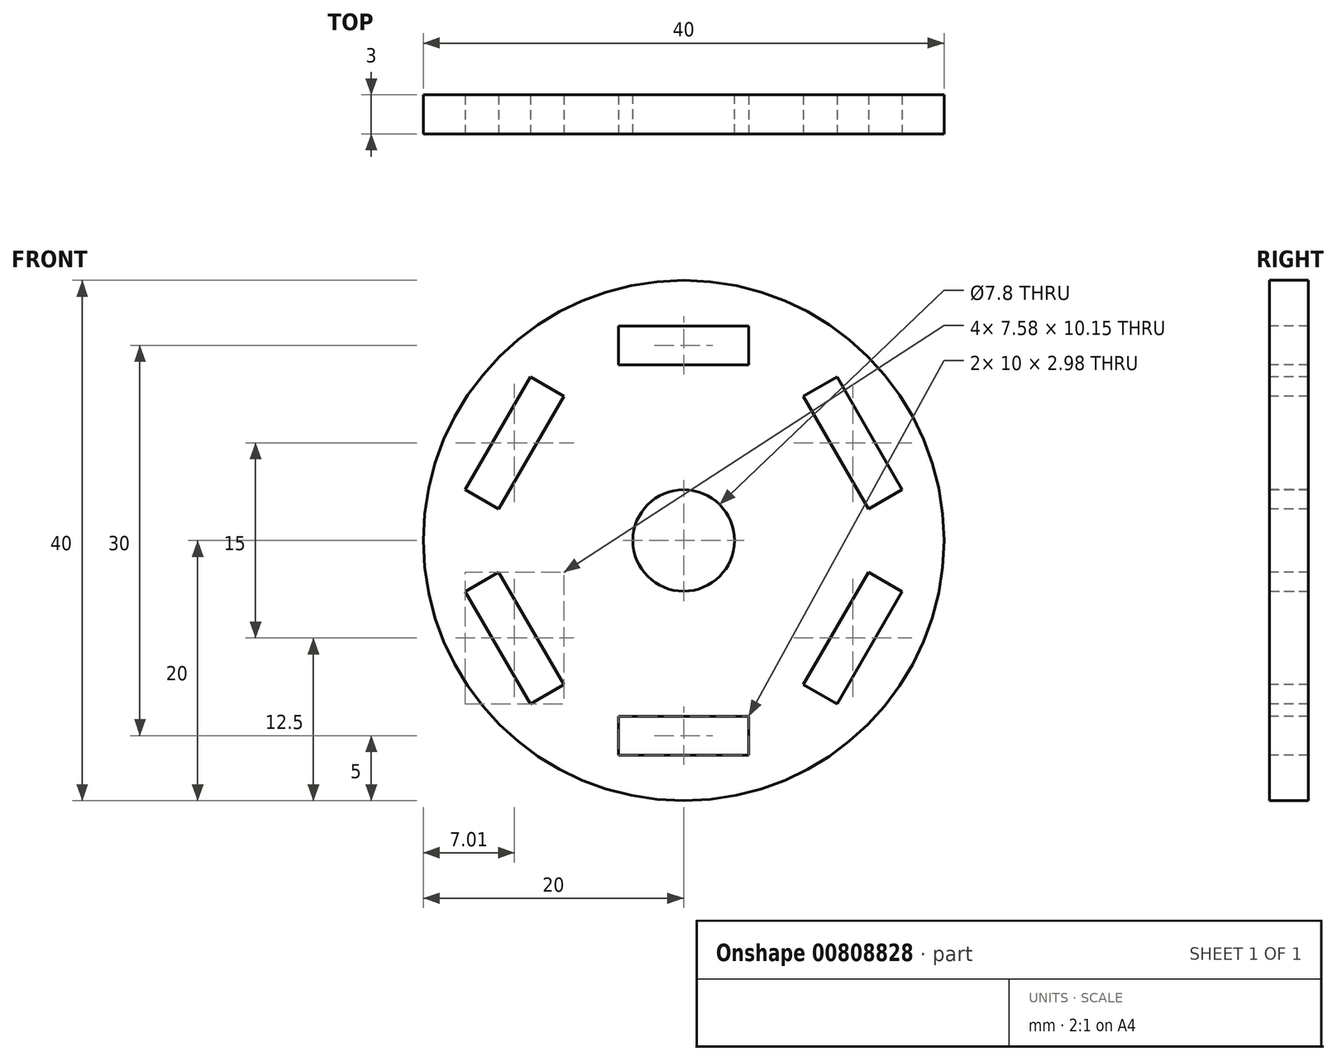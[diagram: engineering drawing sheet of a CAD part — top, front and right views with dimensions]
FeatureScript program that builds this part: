
annotation { "Feature Type Name" : "Feature", "Feature Type Description" : "" }
export const myFeature = defineFeature(function(context is Context, id is Id, definition is map)
    precondition{}
    {
        {
            var Q0;
            Q0=qCreatedBy(makeId("Front.planeOp"),FACE);
            var sketch = newSketch(context, id + "F0", { "sketchPlane" : qUnion([Q0])});
            skCircle(sketch, "E0", {"center": v(0, 0) * mm, "radius": 20 * mm});
            skCircle(sketch, "E1", {"center": v(0, 0) * mm, "radius": 3.9 * mm});
            skSolve(sketch);
        }
        {
            var Q0;
            Q0=qSketchRegion(id+"F0",true);
            extrude(context, id + "F1", {"entities" : qUnion([Q0]), "depth" : 3 * mm, "offsetDistance" : 25 * mm});
        }
        {
            var Q0;
            Q0=makeQuery(id+"F1.opExtrude","CAP_FACE",FACE,{"disambiguationData":[OSD([sQuery(id+"F0.wireOp",EDGE,"E0"),sQuery(id+"F0.wireOp",EDGE,"E1")])],"isStart":false});
            var sketch = newSketch(context, id + "F2", { "sketchPlane" : qUnion([Q0])});
            skLineSegment(sketch, "E2.bottom", {"start": v(-5, -13.5) * mm, "end": v(5, -13.5) * mm});
            skLineSegment(sketch, "E2.top", {"start": v(-5, -16.49) * mm, "end": v(5, -16.49) * mm});
            skLineSegment(sketch, "E2.left", {"start": v(-5, -13.5) * mm, "end": v(-5, -16.49) * mm});
            skLineSegment(sketch, "E2.right", {"start": v(5, -13.5) * mm, "end": v(5, -16.49) * mm});
            skPoint(sketch, "E2.middle", {"position": v(0, -15) * mm});
            skLineSegment(sketch, "E3.1.0", {"start": v(9.2, -11.09) * mm, "end": v(14.2, -2.42) * mm});
            skLineSegment(sketch, "E3.1.1", {"start": v(9.2, -11.09) * mm, "end": v(11.78, -12.58) * mm});
            skLineSegment(sketch, "E3.1.2", {"start": v(11.78, -12.58) * mm, "end": v(16.78, -3.91) * mm});
            skLineSegment(sketch, "E3.1.3", {"start": v(14.2, -2.42) * mm, "end": v(16.78, -3.91) * mm});
            skLineSegment(sketch, "E3.2.0", {"start": v(14.2, 2.42) * mm, "end": v(9.2, 11.09) * mm});
            skLineSegment(sketch, "E3.2.1", {"start": v(14.2, 2.42) * mm, "end": v(16.78, 3.91) * mm});
            skLineSegment(sketch, "E3.2.2", {"start": v(16.78, 3.91) * mm, "end": v(11.78, 12.58) * mm});
            skLineSegment(sketch, "E3.2.3", {"start": v(9.2, 11.09) * mm, "end": v(11.78, 12.58) * mm});
            skLineSegment(sketch, "E3.3.0", {"start": v(5, 13.5) * mm, "end": v(-5, 13.5) * mm});
            skLineSegment(sketch, "E3.3.1", {"start": v(5, 13.5) * mm, "end": v(5, 16.49) * mm});
            skLineSegment(sketch, "E3.3.2", {"start": v(5, 16.5) * mm, "end": v(-5, 16.5) * mm});
            skLineSegment(sketch, "E3.3.3", {"start": v(-5, 13.51) * mm, "end": v(-5, 16.49) * mm});
            skLineSegment(sketch, "E3.4.0", {"start": v(-9.2, 11.09) * mm, "end": v(-14.2, 2.42) * mm});
            skLineSegment(sketch, "E3.4.1", {"start": v(-9.2, 11.09) * mm, "end": v(-11.78, 12.58) * mm});
            skLineSegment(sketch, "E3.4.2", {"start": v(-11.78, 12.58) * mm, "end": v(-16.78, 3.91) * mm});
            skLineSegment(sketch, "E3.4.3", {"start": v(-14.2, 2.42) * mm, "end": v(-16.78, 3.91) * mm});
            skPoint(sketch, "E3.center", {"position": v(0, 0) * mm});
            skLineSegment(sketch, "E4.1.5.0", {"start": v(-14.2, -2.42) * mm, "end": v(-9.2, -11.09) * mm});
            skLineSegment(sketch, "E4.3.5.0", {"start": v(-14.2, -2.42) * mm, "end": v(-16.78, -3.91) * mm});
            skLineSegment(sketch, "E4.6.5.0", {"start": v(-16.78, -3.91) * mm, "end": v(-11.78, -12.58) * mm});
            skLineSegment(sketch, "E4.9.5.0", {"start": v(-9.2, -11.09) * mm, "end": v(-11.78, -12.58) * mm});
            skSolve(sketch);
        }
        {
            var Q0;
            Q0=qSketchRegion(id+"F2",true);
            extrude(context, id + "F3", {"entities" : qUnion([Q0]), "operationType" : NewBodyOperationType.REMOVE, "oppositeDirection" : true, "depth" : 25 * mm, "offsetDistance" : 25 * mm});
        }
    });
